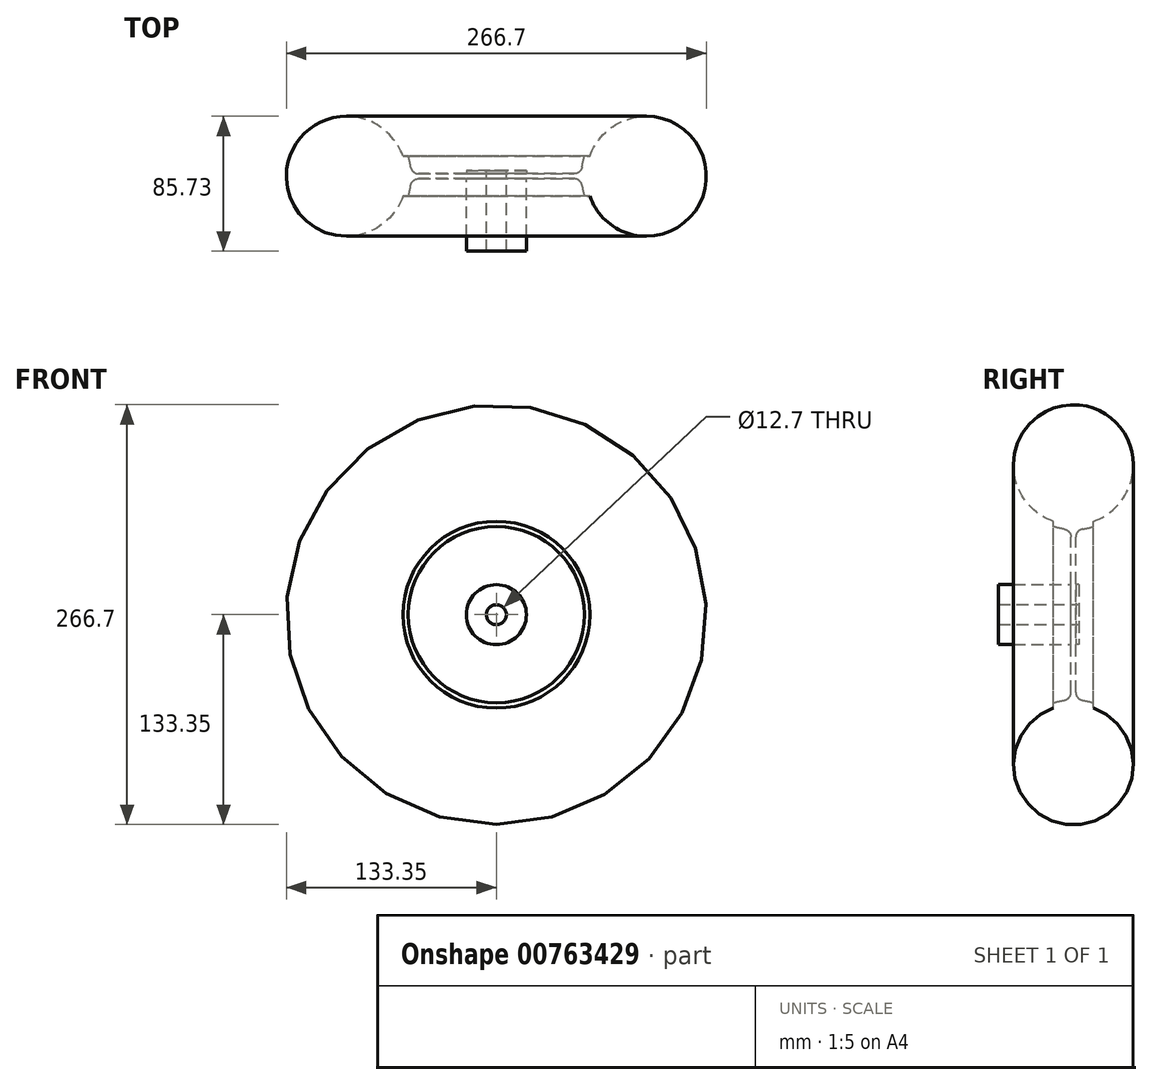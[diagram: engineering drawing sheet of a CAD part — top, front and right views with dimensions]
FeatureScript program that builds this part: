
annotation { "Feature Type Name" : "Feature", "Feature Type Description" : "" }
export const myFeature = defineFeature(function(context is Context, id is Id, definition is map)
    precondition{}
    {
        {
            var Q0;
            Q0=qCreatedBy(makeId("Top.planeOp"),FACE);
            var sketch = newSketch(context, id + "F0", { "sketchPlane" : qUnion([Q0])});
            skCircle(sketch, "E0", {"center": v(-95.25, 0) * mm, "radius": 38.1 * mm});
            skLineSegment(sketch, "E1.bottom", {"start": v(0, 0) * mm, "end": v(-63.15, 0) * mm});
            skLineSegment(sketch, "E1.top", {"start": v(0, 1.59) * mm, "end": v(-63.15, 1.59) * mm});
            skLineSegment(sketch, "E1.left", {"start": v(0, 0) * mm, "end": v(0, 1.59) * mm});
            skLineSegment(sketch, "E1.right", {"start": v(-63.15, 0) * mm, "end": v(-63.15, 1.59) * mm});
            skLineSegment(sketch, "E2.MirrorCS", {"start": v(0, 0) * mm, "end": v(0, -1.59) * mm});
            skLineSegment(sketch, "E3.MirrorCS", {"start": v(-63.15, 0) * mm, "end": v(-63.15, -1.59) * mm});
            skLineSegment(sketch, "E4.MirrorCS", {"start": v(0, -1.59) * mm, "end": v(-63.15, -1.59) * mm});
            skLineSegment(sketch, "E5", {"start": v(-59.33, 12.7) * mm, "end": v(-55.98, 12.7) * mm});
            skLineSegment(sketch, "E6.MirrorCS", {"start": v(-59.33, -12.7) * mm, "end": v(-55.98, -12.7) * mm});
            skArc(sketch, "E7", {"start": v(-55.98, -12.7) * mm, "mid": v(-53.98, 0) * mm, "end": v(-55.98, 12.7) * mm});
            skPoint(sketch, "E8.orphan", {"position": v(-49.06, -12.7) * mm});
            skPoint(sketch, "E9.orphan", {"position": v(-61.59, -12.7) * mm});
            skPoint(sketch, "E10.orphan", {"position": v(-61.59, 12.7) * mm});
            skPoint(sketch, "E11.orphan", {"position": v(-49.06, 12.7) * mm});
            skSolve(sketch);
        }
        {
            var Q0;
            {var subQ0=sQuery(id+"F0.wireOp",EDGE,"E5");Q0=makeQuery(id+"F0.imprint","IMPRINT",FACE,{"disambiguationData":[TD([[makeQuery(id+"F0.imprint","IMPRINT",EDGE,{"derivedFrom":subQ0}),-1.0]])]});}
            var Q1;
            {var subQ0=sQuery(id+"F0.wireOp",EDGE,"E6.MirrorCS");Q1=makeQuery(id+"F0.imprint","IMPRINT",FACE,{"disambiguationData":[TD([[makeQuery(id+"F0.imprint","IMPRINT",EDGE,{"derivedFrom":subQ0}),1.0]])]});}
            var Q2;
            {var subQ0=sQuery(id+"F0.wireOp",EDGE,"E1.left");Q2=makeQuery(id+"F0.imprint","IMPRINT",FACE,{"disambiguationData":[TD([[makeQuery(id+"F0.imprint","IMPRINT",EDGE,{"derivedFrom":subQ0}),1.0]])]});}
            var Q3;
            {var subQ5=sQuery(id+"F0.wireOp",EDGE,"E1.right");Q3=makeQuery(id+"F0.imprint","IMPRINT",FACE,{"disambiguationData":[TD([[makeQuery(id+"F0.imprint","IMPRINT",EDGE,{"derivedFrom":subQ5}),-1.0]])]});}
            var Q4;
            {var subQ0=sQuery(id+"F0.wireOp",EDGE,"E1.top");var subQ1=sQuery(id+"F0.wireOp",EDGE,"E0");var subQ2=makeQuery(id+"F0.imprint","INTERSECT",VERTEX,{"derivedFrom":[subQ1,subQ0]});Q4=makeQuery(id+"F0.imprint","IMPRINT",FACE,{"disambiguationData":[TD([[makeQuery(id+"F0.imprint","IMPRINT",EDGE,{"disambiguationData":[TD([[subQ2,1.0]])],"derivedFrom":subQ1}),-1.0]])]});}
            var Q5;
            {var subQ4=sQuery(id+"F0.wireOp",EDGE,"E1.right");Q5=makeQuery(id+"F0.imprint","IMPRINT",FACE,{"disambiguationData":[TD([[makeQuery(id+"F0.imprint","IMPRINT",EDGE,{"derivedFrom":subQ4}),1.0]])]});}
            var Q6;
            {var subQ5=sQuery(id+"F0.wireOp",EDGE,"E3.MirrorCS");Q6=makeQuery(id+"F0.imprint","IMPRINT",FACE,{"disambiguationData":[TD([[makeQuery(id+"F0.imprint","IMPRINT",EDGE,{"derivedFrom":subQ5}),1.0]])]});}
            var Q7;
            {var subQ0=sQuery(id+"F0.wireOp",EDGE,"E2.MirrorCS");Q7=makeQuery(id+"F0.imprint","IMPRINT",FACE,{"disambiguationData":[TD([[makeQuery(id+"F0.imprint","IMPRINT",EDGE,{"derivedFrom":subQ0}),-1.0]])]});}
            var Q8;
            {var subQ0=sQuery(id+"F0.wireOp",EDGE,"E1.bottom");var subQ1=sQuery(id+"F0.wireOp",EDGE,"E0");var subQ2=makeQuery(id+"F0.imprint","INTERSECT",VERTEX,{"derivedFrom":[subQ1,subQ0]});Q8=makeQuery(id+"F0.imprint","IMPRINT",FACE,{"disambiguationData":[TD([[makeQuery(id+"F0.imprint","IMPRINT",EDGE,{"disambiguationData":[TD([[subQ2,1.0]])],"derivedFrom":subQ1}),-1.0]])]});}
            var Q9;
            Q9=sQuery(id+"F0.wireOp",EDGE,"E1.left");
            revolve(context, id + "F1", {"surfaceOperationType" : NewSurfaceOperationType.NEW, "entities" : qUnion([Q0, Q1, Q2, Q3, Q4, Q5, Q6, Q7, Q8]), "axis" : qUnion([Q9]), "revolveType" : RevolveType.FULL});
        }
        {
            var Q0;
            Q0=makeQuery(id+"F1.opRevolve","SWEPT_EDGE",EDGE,{"disambiguationData":[OSD([sQuery(id+"F0.wireOp",EDGE,"E4.MirrorCS"),sQuery(id+"F0.wireOp",EDGE,"E7")])]});
            var Q1;
            Q1=makeQuery(id+"F1.opRevolve","SWEPT_EDGE",EDGE,{"disambiguationData":[OSD([sQuery(id+"F0.wireOp",EDGE,"E1.top"),sQuery(id+"F0.wireOp",EDGE,"E7")])]});
            fillet(context, id + "F2", {"entities" : qUnion([Q0, Q1]), "radius" : 5.08 * mm, "tangentPropagation" : true, "allowEdgeOverflow" : false});
        }
        {
            var Q0;
            Q0=makeQuery(id+"F1.opRevolve","SWEPT_FACE",FACE,{"disambiguationData":[OSD([sQuery(id+"F0.wireOp",EDGE,"E4.MirrorCS")])]});
            var sketch = newSketch(context, id + "F3", { "sketchPlane" : qUnion([Q0])});
            skCircle(sketch, "E12", {"center": v(0, 0) * mm, "radius": 19.05 * mm});
            skSolve(sketch);
        }
        {
            var Q0;
            Q0=makeQuery(id+"F3.imprint","IMPRINT",FACE,{"disambiguationData":[TD([[makeQuery(id+"F3.imprint","IMPRINT",EDGE,{"derivedFrom":sQuery(id+"F3.wireOp",EDGE,"E12")}),1.0]])]});
            extrude(context, id + "F4", {"entities" : qUnion([Q0]), "operationType" : NewBodyOperationType.ADD, "depth" : 46.04 * mm, "offsetDistance" : 25.4 * mm});
        }
        {
            var Q0;
            Q0=makeQuery(id+"F1.opRevolve","SWEPT_FACE",FACE,{"disambiguationData":[OSD([sQuery(id+"F0.wireOp",EDGE,"E1.top")])]});
            var sketch = newSketch(context, id + "F5", { "sketchPlane" : qUnion([Q0])});
            skCircle(sketch, "E13", {"center": v(0, 0) * mm, "radius": 19.05 * mm});
            skCircle(sketch, "E14", {"center": v(0, 0) * mm, "radius": 6.35 * mm});
            skSolve(sketch);
        }
        {
            var Q0;
            Q0=makeQuery(id+"F5.imprint","IMPRINT",FACE,{"disambiguationData":[TD([[makeQuery(id+"F5.imprint","IMPRINT",EDGE,{"derivedFrom":sQuery(id+"F5.wireOp",EDGE,"E13")}),1.0]])]});
            extrude(context, id + "F6", {"entities" : qUnion([Q0]), "operationType" : NewBodyOperationType.REMOVE, "oppositeDirection" : true, "depth" : 2.03 * mm, "offsetDistance" : 25.4 * mm});
        }
        {
            var Q0;
            Q0=makeQuery(id+"F6.boolean.opBoolean","SPLIT",FACE,{"disambiguationData":[TD([makeQuery(id+"F6.opExtrude","SWEPT_FACE",FACE,{"disambiguationData":[OSD([sQuery(id+"F5.wireOp",EDGE,"E14")])]})])],"derivedFrom":makeQuery(id+"F1.opRevolve","SWEPT_FACE",FACE,{"disambiguationData":[OSD([sQuery(id+"F0.wireOp",EDGE,"E1.top")])]})});
            extrude(context, id + "F7", {"entities" : qUnion([Q0]), "operationType" : NewBodyOperationType.REMOVE, "oppositeDirection" : true, "depth" : 50.8 * mm, "offsetDistance" : 25.4 * mm});
        }
        {
            var Q0;
            Q0=makeQuery(id+"F6.boolean.opBoolean","COPY",FACE,{"derivedFrom":makeQuery(id+"F6.opExtrude","CAP_FACE",FACE,{"disambiguationData":[OSD([sQuery(id+"F5.wireOp",EDGE,"E13"),sQuery(id+"F5.wireOp",EDGE,"E14")])],"isStart":false})});
            extrude(context, id + "F8", {"entities" : qUnion([Q0]), "operationType" : NewBodyOperationType.ADD, "depth" : 4.06 * mm, "offsetDistance" : 25.4 * mm});
        }
    });
